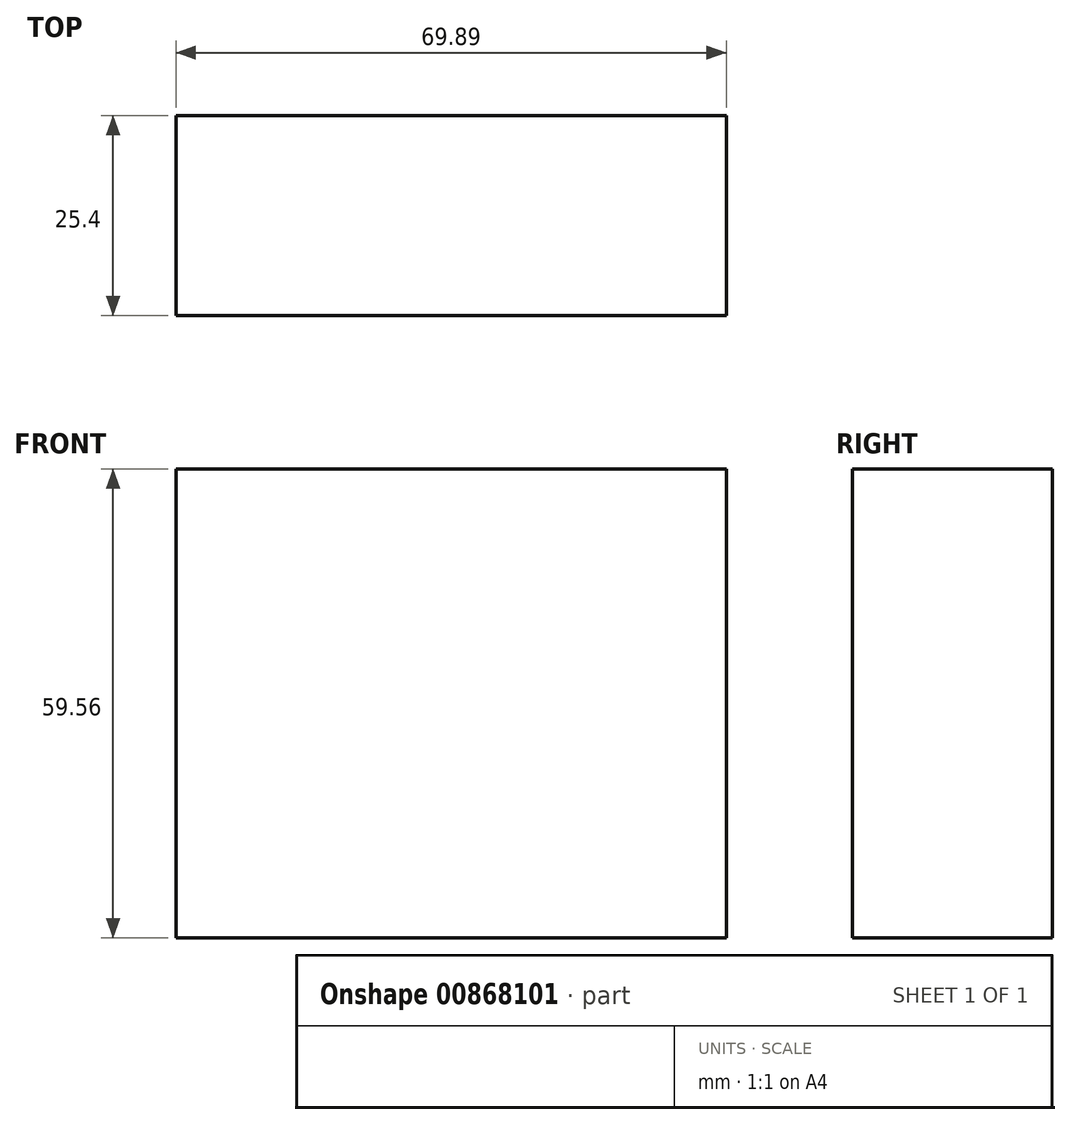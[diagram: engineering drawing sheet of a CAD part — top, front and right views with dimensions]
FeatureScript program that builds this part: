
annotation { "Feature Type Name" : "Feature", "Feature Type Description" : "" }
export const myFeature = defineFeature(function(context is Context, id is Id, definition is map)
    precondition{}
    {
        {
            var Q0;
            Q0=qCreatedBy(makeId("Front.planeOp"),FACE);
            var sketch = newSketch(context, id + "F0", { "sketchPlane" : qUnion([Q0])});
            skLineSegment(sketch, "E0.bottom", {"start": v(-30.54, 28.23) * mm, "end": v(39.35, 28.23) * mm});
            skLineSegment(sketch, "E0.top", {"start": v(-30.54, -31.33) * mm, "end": v(39.35, -31.33) * mm});
            skLineSegment(sketch, "E0.left", {"start": v(-30.54, 28.23) * mm, "end": v(-30.54, -31.33) * mm});
            skLineSegment(sketch, "E0.right", {"start": v(39.35, 28.23) * mm, "end": v(39.35, -31.33) * mm});
            skSolve(sketch);
        }
        {
            var Q0;
            Q0=makeQuery(id+"F0.imprint","IMPRINT",FACE,{"disambiguationData":[TD([[makeQuery(id+"F0.imprint","IMPRINT",EDGE,{"derivedFrom":sQuery(id+"F0.wireOp",EDGE,"E0.bottom")}),-1.0]])]});
            extrude(context, id + "F1", {"entities" : qUnion([Q0]), "depth" : 25.4 * mm, "offsetDistance" : 25.4 * mm});
        }
    });
